# Revit family: Urinal-Wall_Mount-American_Standard-Decorum-604X.001EC.020
name_source: partatom
category: Plumbing Fixtures
units: mm (PartAtom-declared; Revit-internal decimal feet)

## family parameters
Cut with Voids When Loaded = No
Host = Face
OmniClass Number = 23.45.05.21.11.21
OmniClass Title = Urinals
Part Type = Normal
Room Calculation Point = No
Round Connector Dimension = Use Radius
Shared = Yes

## types (2) — shared parameters
ADA Compliant = Yes
Assembly Code = D2010210
CEC Compliant = Yes
CW Connection = Yes
CWFU = 5
CalGreen Compliant = Yes
Cold Water Connection Diameter = 3/4"
Cold Water Connection Height = 11 1/2"
Cold Water Connection Radius = 3/8"
Cold Water Connection Width = 4 3/4"
Compliance Certifications = Meets or Exceeds ASME A112.19.2-2008/CSA B45.1-08 for Vitreous China Fixtures
Default Elevation = 24"
Finish = Vitreous China-American Standard-020-White
Flush Rate = 0.125 GPF (0.47 Lpf)
HW Connection = No
Height = 21 1/2"
Installation Type = Wall Mounted
Length = 14"
Manufacturer = American Standard
Material = Vitreous China-American Standard-020-White
Price = Prices may vary. Please consult Manufacturer Representative for most up-to-date price list.
Product Documentation Link = https://americanstandard.box.com
Product Page URL = https://www.americanstandard-us.com
Revised Date = 03/14/2022
Strainer Material = Metal-American Standard-Chrome Plated
URL = http://www.americanstandard-us.com
Vent Connection = No
WFU = 5
Waste Connection = Yes
Waste Connection Diameter = 2"
Waste Connection Height = 2 1/2"
Waste Connection Radius = 1"
Width = 13 5/16"
Working Pressure = Between 20 psi at valve when flushing and 80 psi static
zero-valued in all types: HWFU

## per-type parameters (varying)
| type | Back Spud | Back Spud Connection Radius | Back Spud Inlet Connection Description | Description | Top Spud | Top Spud Connection Radius | Top Spud Inlet Connection Description |
| 6042.001EC.020 | No | 0" |  | Decorum® 0.125 gpf/0.47 Lpf Top Spud Urinal with EverClean® | Yes | 3/8" | 3/4 in. Top Inlet Supply Connection |
| 6043.001EC.020 | Yes | 3/8" | 3/4 in. Back Inlet Supply Connection | Decorum® 0.125 gpf/0.47 Lpf Back Spud Urinal With EverClean | No | 0" |  |

note: column(s) folded — value = type name in every type: Model

## geometry (parser evidence)
native form markers: Sweep x2
no freeform markers — native parametric forms only
